# Revit family: IS_iLifeB_T4614_BIM_NL
name_source: partatom
category: Plumbing Fixtures
units: mm (PartAtom-declared; Revit-internal decimal feet)

## family parameters
Always vertical = No
Cut with Voids When Loaded = No
OmniClass Number = 23.45.05.21.11.11
OmniClass Title = Water Operated Water Closets
Part Type = Normal
Room Calculation Point = No
Round Connector Dimension = Use Diameter
Shared = No
Work Plane-Based = No

## types (4) — shared parameters
Accessories = https://www.idealstandard.nl
Afmetingen = 354 x 540 x 337 mm
AfstandsEenheid = Millimeter
AreaMeasurement = Internal
AreaUnits = millimetres
AssetType = Fixed
Auteur = Ideal Standard
BIMObjectName = IS_IdealStandard_WCpans_i.lifeB_T4614
BIMobject category = Toilets
BIMobject category code = toilets
BIMobject main category = Sanitary
BIMobject main category code = sanitary
Beschrijvinggarantie = Herstellergarantie
BimObjectNaam = IS_IdealStandard_WCpans_i.lifeB_T4614
Brand = Ideal Standard
Brand url = https://www.idealstandard.nl
Breedte = 354.306046
Category = Sanitary
Classification = WC Pans
ConnectionType = Plumbing
CurrencyUnit = €
CurrentRevision = 1
Date of publishing = 22/07/2022
Diepte = 540 mm
DurationUnit = Years
DuurEenheid = Jahre
Edition number = 1
ElementType = Fixed
ExpectedLife = 99
Features = wallhung bowl, RimLS+, hidden fixation, Easyfix+, in carton box, EU pallet
GarantieduurInstallatie = https://www.idealstandard.nl
Garantieonderdelen = https://www.idealstandard.nl
Garantieunits = Jahre
GemaaktOp = 22/07/2022
Help = https://www.idealstandard.nl
Hoogte = 337.117536078484
Hulp = https://www.idealstandard.nl
IFC Classification = Sanitary Terminal
IfcExportAs = IfcSanitaryTerminalType
IfcExportType = TOILETPAN
Installatieinstructies = https://www.idealstandard.nl
Installation instructions = https://www.idealstandard.nl
InstallationInstructions = https://www.idealstandard.nl
Lengte = 540 mm
LinearUnits = millimetres
MaintenanceInformation = https://www.idealstandard.nl
Manufacturer = Ideal Standard
Manufacturer name = Ideal Standard
ManufacturerURL = https://www.idealstandard.nl
Materiaal = Schamotte
Material = Fireclay
Material main = Fireclay
Merk = Ideal Standard
ModelReference = IS I.LIFE B Wall Hung WC Bowl Boxed
NBS Reference Code = 45-35-70/384
NBS Reference Description = WC pans
Name = WCpans_i.lifeB_T4614_IdealStandard
NettWeight = 22.5
Nettogewicht = 22.5
NominalDepth = 540 mm
NominalHeight = 337 mm
NominalLength = 540 mm
NominalWidth = 354 mm
OmniClass Code = 23-31 19 00
OmniClass Description = Toilets
OppervlakteEenheid = Millimeter
PanMaterial = Finefire Clay
PanMounting = Wall Hung
PredefinedType = WC Pans
Product Guid = b068d118-ca57-4594-9c8f-18fe2636707e
Product SKU = T4614
Product certification = https://www.idealstandard.nl
Product data url = https://bimobject.com
Product family = I.Life B
Product group = Sanitary
Product name = IS I.LIFE B Wall Hung WC Bowl Boxed
Product url = https://www.idealstandard.nl
ProductInformation = https://www.idealstandard.nl
Productinformatie = https://www.idealstandard.nl
QR code = http://bimobject.com
Revisie = 1
SeatHasCover = No
SeatMaterial = Acrylic
Shape = sculptured
Size = 354 x 540 x 337 mm
Space = Internal
SpareParts = https://www.idealstandard.nl
Technical description = https://www.idealstandard.nl
Telefoonnummer = 077 355 08 08
Toepassing = WC Pans
ToiletPanType = Wall -Hung WC Bowl
ToiletType = Wall -Hung WC Bowl
Typeconnectie = Installation
UNSPSC Code = 301815
URL = https://www.idealstandard.nl
Uniclass 2015 Code = Pr_40_20_93_94
Uniclass 2015 Name = WC pans
Uniclass2015Beschrijving = WC pans
Uniclass2015Code = Pr_40_20_93_94
Uniclass2015Referentie = Pr_40_20_93_94
Uniclass2015Title = WC pans
Uniclass2015Version = v1.26
Urlproducent = https://www.idealstandard.nl
ValutaEenheid = Euro
Versie = 1
Version = 1
Verwachtelevensduur = 5
VolumeUnits = Liters
Volumeunits = Liter
Vorm = geformt
WRASURL = https://www.wrasapprovals.co.uk
WarrantyDescription = manufacturer warranty
WarrantyDurationUnit = Years
Weight Net (Kg) = 22.5
Wisselstukken = https://www.idealstandard.nl
Youtube clip = https://www.youtube.com
zero-valued in all types: BrutoGewicht, Cost, Default Elevation, Vervangingskosten

## per-type parameters (varying)
| type | Afwerking | Artikelnummer | Artikelomschrijving | Artikelreferentie | BarCode | Barcode | Color | Description | Eigenschappen | Finish | GTIN code | Kleur | Kleurwc | MainColor | Model | ModelNumber | PanColor | Referentie | SeatColor |
| T461401 - IS I.LIFE B Wall Hung WC Bowl Boxed - White | Weiss | T461401 | Ideal Standard i.life B, wandhängendes Becken, RimLS+, verdeckte Befestigung, Easyfix+, weiß, im Karton, EU-Palette | T461401 | 8014140486008 | 8014140486008 | White | Ideal Standard i.life B, wallhung bowl, RimLS+, hidden fixation, Easyfix+, white, in carton box, EU pallet | Wandschale, RimLS+, verdeckte Befestigung, Easyfix+, weiß, im Karton, EU-Palette | White | 8014140486008 | Weiss | Weiss | White | T461401 | T461401 | White | Ideal Standard i.life B, close coupled toilet, RimLS+, horizontal outlet, L-shape floor fixation | White |
| T4614MA - IS I.LIFE B Wall Hung WC Bowl Boxed - White IP | Ideal plus Weiß | T4614MA | Ideal Standard i.life B, wandhängendes Becken, RimLS+, verdeckte Befestigung, Easyfix+, weiß, im Karton, EU-Palette | T4614MA | 8014140486794 | 8014140486794 | Ideal plus White | Ideal Standard i.life B, wallhung bowl, RimLS+, hidden fixation, Easyfix+, white, in carton box, EU pallet | Wandschale, RimLS+, verdeckte Befestigung, Easyfix+, weiß, im Karton, EU-Palette | Ideal plus White | 8014140486794 | Ideal plus Weiß | Ideal plus Weiß | Ideal plus White | T4614MA | T4614MA | Ideal plus White | IS I.LIFE B Wall Hung WC Bowl Boxed | Ideal plus White |
| T4614HY - IS I.LIFE B Wall Hung WC Bowl Boxed - Antibacterial glaze Smartguard+ | Weiss Smartguard+ | T4614HY | Ideal Standard i.life B, wandhängendes Becken, RimLS+, verdeckte Befestigung, Easyfix+, weiß, im Karton, EU-Palette | T4614HY | 8014140514657 | 8014140514657 | White Smartguard+ | Ideal Standard i.life B, wallhung bowl, RimLS+, hidden fixation, Easyfix+, antibacterial glaze Smartguard+, in carton box, EU pallet | Wandschale, RimLS+, verdeckte Befestigung, Easyfix+, antibakterielle Glasur Smartguard+, im Karton, EU-Palette | White Smartguard+ | 8014140514657 | Weiss Smartguard+ | Weiss Smartguard+ | White Smartguard+ | T4614HY | T4614HY | White Smartguard+ | IS I.LIFE B Wall Hung WC Bowl Boxed | White Smartguard+ |
| T461458 - IS I.LIFE B Wall Hung WC Bowl Boxed - Glossy grey | Glänzend grau | T461458 | Ideal Standard i.life B, wandhängendes Becken, RimLS+, verdeckte Befestigung, Easyfix+, glänzend grau, im Karton, EU-Palette | T461458 | 8014140511632 | 8014140511632 | Glossy grey | Ideal Standard i.life B, wallhung bowl, RimLS+, hidden fixation, Easyfix+, glossy grey, in carton box, EU pallet | Wandschale, RimLS+, verdeckte Befestigung, Easyfix+, weiß, im Karton, EU-Palette | Glossy grey | 8014140511632 | Glänzend grau | Glänzend grau | Glossy grey | T461458 | T461458 | Glossy grey | Ideal Standard i.life B, close coupled toilet, RimLS+, horizontal outlet, L-shape floor fixation | Glossy grey |

## geometry (parser evidence)
native form markers: Blend x4, Sweep x3
no freeform markers — native parametric forms only
